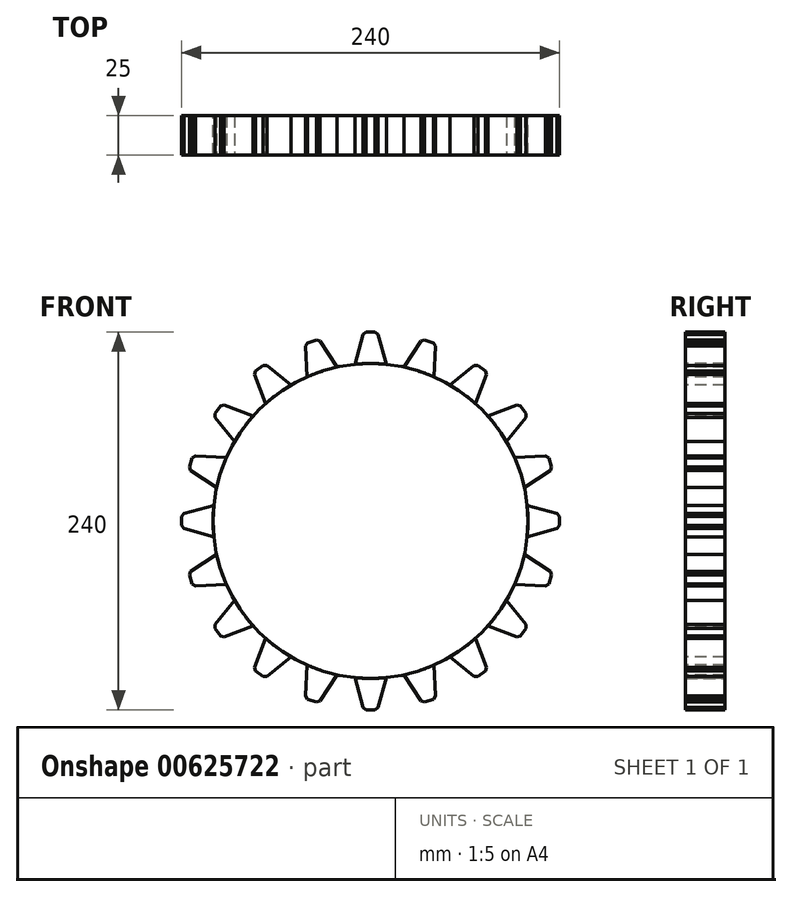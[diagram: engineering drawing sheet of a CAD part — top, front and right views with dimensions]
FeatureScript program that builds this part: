
annotation { "Feature Type Name" : "Feature", "Feature Type Description" : "" }
export const myFeature = defineFeature(function(context is Context, id is Id, definition is map)
    precondition{}
    {
        {
            var Q0;
            Q0=qCreatedBy(makeId("Front.planeOp"),FACE);
            var sketch = newSketch(context, id + "F0", { "sketchPlane" : qUnion([Q0])});
            skCircle(sketch, "E0", {"center": v(0, 0) * mm, "radius": 100 * mm});
            skSolve(sketch);
        }
        {
            var Q0;
            Q0=makeQuery(id+"F0.imprint","IMPRINT",FACE,{"disambiguationData":[TD([[makeQuery(id+"F0.imprint","IMPRINT",EDGE,{"derivedFrom":sQuery(id+"F0.wireOp",EDGE,"E0")}),1.0]])]});
            extrude(context, id + "F1", {"entities" : qUnion([Q0]), "depth" : 25 * mm, "offsetDistance" : 25 * mm});
        }
        {
            var Q0;
            Q0=makeQuery(id+"F1.opExtrude","CAP_FACE",FACE,{"disambiguationData":[OSD([sQuery(id+"F0.wireOp",EDGE,"E0")])],"isStart":false});
            var sketch = newSketch(context, id + "F2", { "sketchPlane" : qUnion([Q0])});
            skLineSegment(sketch, "E1", {"start": v(-10, 99.5) * mm, "end": v(-4.5, 120) * mm});
            skLineSegment(sketch, "E2", {"start": v(-4.5, 120) * mm, "end": v(4.5, 120) * mm});
            skLineSegment(sketch, "E3", {"start": v(4.5, 120) * mm, "end": v(10, 99.5) * mm});
            skLineSegment(sketch, "E4", {"start": v(-10, 99.5) * mm, "end": v(10, 99.5) * mm});
            skSolve(sketch);
        }
        {
            var Q0;
            {var subQ0=sQuery(id+"F2.wireOp",EDGE,"E1");Q0=makeQuery(id+"F2.imprint","IMPRINT",FACE,{"disambiguationData":[TD([[makeQuery(id+"F2.imprint","IMPRINT",EDGE,{"derivedFrom":subQ0}),-1.0]])]});}
            extrude(context, id + "F3", {"entities" : qUnion([Q0]), "oppositeDirection" : true, "depth" : 25 * mm, "offsetDistance" : 25 * mm});
        }
        {
            var Q0;
            Q0=makeQuery(id+"F3.opExtrude","SWEPT_EDGE",EDGE,{"disambiguationData":[OSD([sQuery(id+"F2.wireOp",EDGE,"E1"),sQuery(id+"F2.wireOp",EDGE,"E2")])]});
            var Q1;
            Q1=makeQuery(id+"F3.opExtrude","SWEPT_EDGE",EDGE,{"disambiguationData":[OSD([sQuery(id+"F2.wireOp",EDGE,"E2"),sQuery(id+"F2.wireOp",EDGE,"E3")])]});
            chamfer(context, id + "F4", {"entities" : qUnion([Q0, Q1]), "width" : 2 * mm, "tangentPropagation" : true});
        }
        {
            var Q0;
            Q0=makeQuery(id+"F3.opExtrude","SWEPT_BODY",BODY,{"disambiguationData":[OSD([sQuery(id+"F0.wireOp",EDGE,"E0"),sQuery(id+"F2.wireOp",EDGE,"E1"),sQuery(id+"F2.wireOp",EDGE,"E2"),sQuery(id+"F2.wireOp",EDGE,"E3")])]});
            var Q1;
            Q1=makeQuery(id+"F1.opExtrude","CAP_EDGE",EDGE,{"disambiguationData":[OSD([sQuery(id+"F0.wireOp",EDGE,"E0")])],"isStart":false});
            circularPattern(context, id + "F5", {"entities" : qUnion([Q0]), "axis" : qUnion([Q1]), "angle" : 360 * degree, "instanceCount" : 20, "equalSpace" : true});
        }
    });
